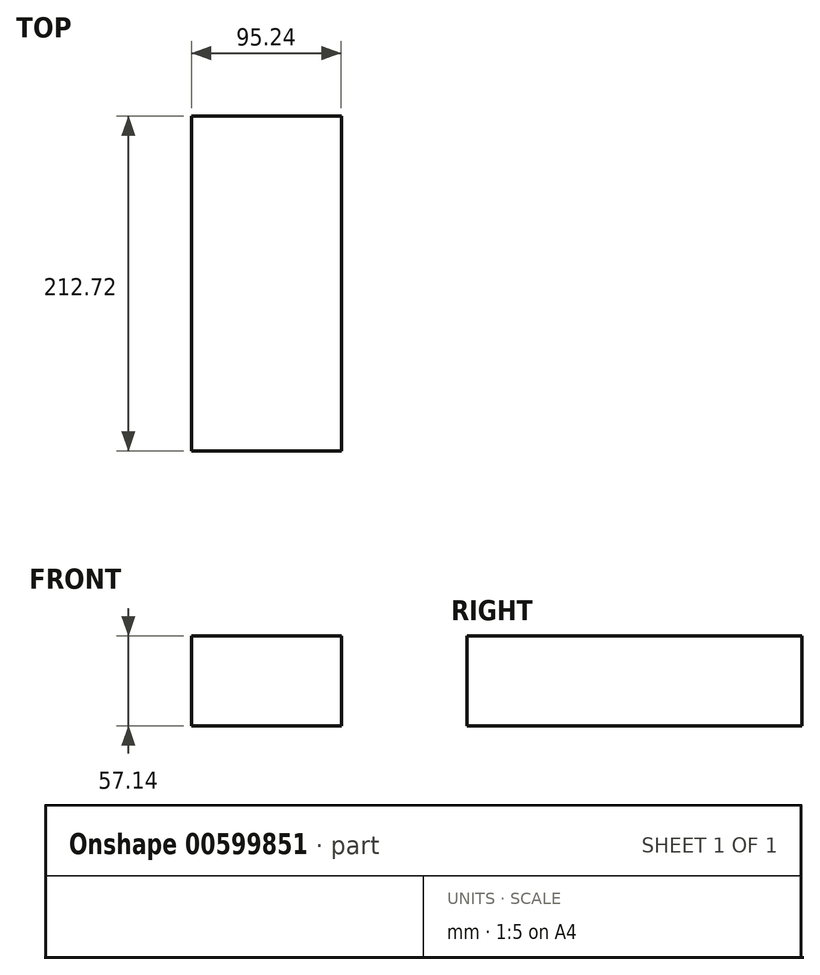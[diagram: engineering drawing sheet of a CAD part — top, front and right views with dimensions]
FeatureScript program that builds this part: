
annotation { "Feature Type Name" : "Feature", "Feature Type Description" : "" }
export const myFeature = defineFeature(function(context is Context, id is Id, definition is map)
    precondition{}
    {
        {
            var Q0;
            Q0=qCreatedBy(makeId("Top.planeOp"),FACE);
            var sketch = newSketch(context, id + "F0", { "sketchPlane" : qUnion([Q0])});
            skLineSegment(sketch, "E0.bottom", {"start": v(47.62, 106.36) * mm, "end": v(-47.63, 106.36) * mm});
            skLineSegment(sketch, "E0.top", {"start": v(47.63, -106.36) * mm, "end": v(-47.62, -106.36) * mm});
            skLineSegment(sketch, "E0.left", {"start": v(47.62, 106.36) * mm, "end": v(47.63, -106.36) * mm});
            skLineSegment(sketch, "E0.right", {"start": v(-47.63, 106.36) * mm, "end": v(-47.62, -106.36) * mm});
            skPoint(sketch, "E0.middle", {"position": v(0, 0) * mm});
            skSolve(sketch);
        }
        {
            var Q0;
            Q0 = qSketchRegion(id + "F0", true);
            extrude(context, id + "F1", {"entities" : qUnion([Q0]), "endBound" : BoundingType.SYMMETRIC, "depth" : 57.15 * mm, "offsetDistance" : 25.4 * mm});
        }
    });
